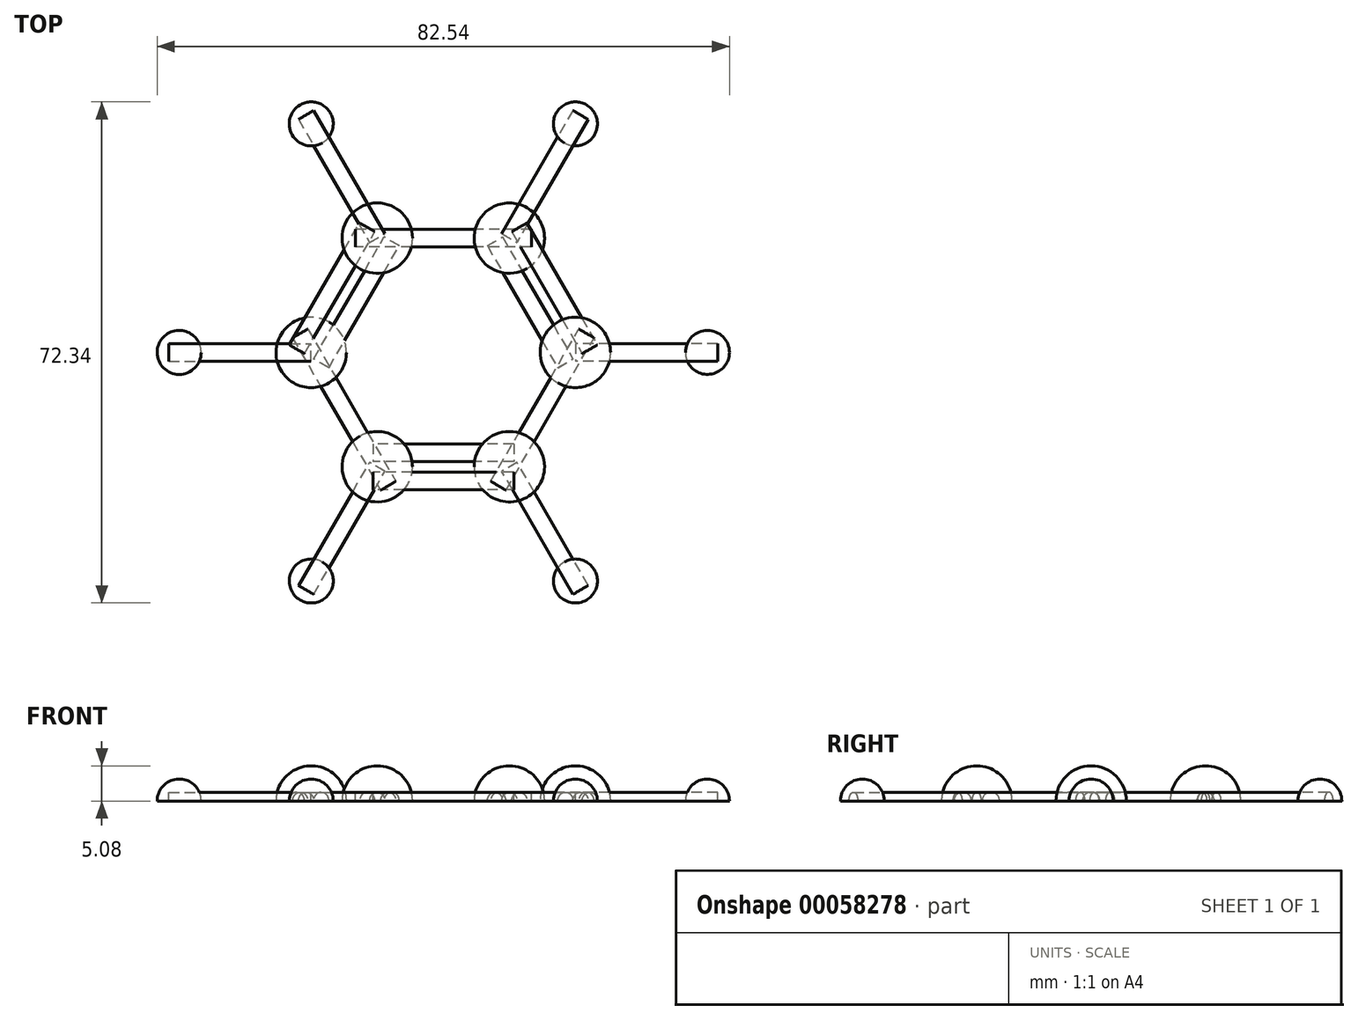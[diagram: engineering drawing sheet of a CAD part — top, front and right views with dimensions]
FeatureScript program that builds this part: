
annotation { "Feature Type Name" : "Feature", "Feature Type Description" : "" }
export const myFeature = defineFeature(function(context is Context, id is Id, definition is map)
    precondition{}
    {
        {
            var Q0;
            Q0=qCreatedBy(makeId("Top.planeOp"),FACE);
            var sketch = newSketch(context, id + "F0", { "sketchPlane" : qUnion([Q0])});
            skCircle(sketch, "E0", {"center": v(-9.53, 16.5) * mm, "radius": 5.08 * mm, "construction": true});
            skCircle(sketch, "E1", {"center": v(9.52, 16.5) * mm, "radius": 5.08 * mm, "construction": true});
            skCircle(sketch, "E2", {"center": v(19.05, 0) * mm, "radius": 5.08 * mm, "construction": true});
            skLineSegment(sketch, "E3", {"start": v(-9.53, 16.5) * mm, "end": v(9.52, 16.5) * mm, "construction": true});
            skLineSegment(sketch, "E4", {"start": v(9.52, 16.5) * mm, "end": v(19.05, 0) * mm, "construction": true});
            skLineSegment(sketch, "E5", {"start": v(19.05, 0) * mm, "end": v(0, 0) * mm, "construction": true});
            skLineSegment(sketch, "E6", {"start": v(9.53, 16.5) * mm, "end": v(0, 0) * mm, "construction": true});
            skLineSegment(sketch, "E7", {"start": v(0, 0) * mm, "end": v(-9.53, 16.5) * mm, "construction": true});
            skLineSegment(sketch, "E8", {"start": v(19.05, 0) * mm, "end": v(38.1, 0) * mm, "construction": true});
            skCircle(sketch, "E9", {"center": v(38.1, 0) * mm, "radius": 3.18 * mm, "construction": true});
            skSolve(sketch);
        }
        {
            var Q0;
            Q0=qCreatedBy(makeId("Top.planeOp"),FACE);
            var sketch = newSketch(context, id + "F1", { "sketchPlane" : qUnion([Q0])});
            skArc(sketch, "E10", {"start": v(-14.6, 16.5) * mm, "mid": v(-9.53, 11.42) * mm, "end": v(-4.45, 16.5) * mm});
            skLineSegment(sketch, "E11", {"start": v(-4.45, 16.5) * mm, "end": v(-14.6, 16.5) * mm});
            skSolve(sketch);
        }
        {
            var Q0;
            Q0=makeQuery(id+"F1.imprint","IMPRINT",FACE,{"disambiguationData":[TD([[makeQuery(id+"F1.imprint","IMPRINT",EDGE,{"derivedFrom":sQuery(id+"F1.wireOp",EDGE,"E10")}),1.0]])]});
            var Q1;
            Q1=sQuery(id+"F1.wireOp",EDGE,"E11");
            revolve(context, id + "F2", {"entities" : qUnion([Q0]), "axis" : qUnion([Q1]), "revolveType" : RevolveType.FULL});
        }
        {
            var Q0;
            Q0=qCreatedBy(makeId("Front.planeOp"),FACE);
            var sketch = newSketch(context, id + "F3", { "sketchPlane" : qUnion([Q0])});
            skLineSegment(sketch, "E12", {"start": v(0, 0) * mm, "end": v(0, 25.4) * mm, "construction": true});
            skSolve(sketch);
        }
        {
            var Q0;
            Q0=makeQuery(id+"F2.opRevolve","SWEPT_BODY",BODY,{"disambiguationData":[OSD([sQuery(id+"F1.wireOp",EDGE,"E10"),sQuery(id+"F1.wireOp",EDGE,"E11")])]});
            var Q1;
            Q1=sQuery(id+"F3.wireOp",EDGE,"E12");
            circularPattern(context, id + "F4", {"entities" : qUnion([Q0]), "axis" : qUnion([Q1]), "angle" : 60 * degree, "instanceCount" : 6, "oppositeDirection" : true});
        }
        {
            var Q0;
            Q0=qCreatedBy(makeId("Top.planeOp"),FACE);
            var sketch = newSketch(context, id + "F5", { "sketchPlane" : qUnion([Q0])});
            skArc(sketch, "E13", {"start": v(34.92, 0) * mm, "mid": v(38.1, -3.17) * mm, "end": v(41.27, 0) * mm});
            skLineSegment(sketch, "E14", {"start": v(34.92, 0) * mm, "end": v(41.27, 0) * mm});
            skSolve(sketch);
        }
        {
            var Q0;
            Q0=makeQuery(id+"F5.imprint","IMPRINT",FACE,{"disambiguationData":[TD([[makeQuery(id+"F5.imprint","IMPRINT",EDGE,{"derivedFrom":sQuery(id+"F5.wireOp",EDGE,"E13")}),1.0]])]});
            var Q1;
            Q1=sQuery(id+"F5.wireOp",EDGE,"E14");
            revolve(context, id + "F6", {"entities" : qUnion([Q0]), "axis" : qUnion([Q1]), "revolveType" : RevolveType.FULL});
        }
        {
            var Q0;
            Q0=makeQuery(id+"F6.opRevolve","SWEPT_BODY",BODY,{"disambiguationData":[OSD([sQuery(id+"F5.wireOp",EDGE,"E13"),sQuery(id+"F5.wireOp",EDGE,"E14")])]});
            var Q1;
            Q1=sQuery(id+"F3.wireOp",EDGE,"E12");
            circularPattern(context, id + "F7", {"entities" : qUnion([Q0]), "axis" : qUnion([Q1]), "angle" : 60 * degree, "instanceCount" : 6});
        }
        {
            var Q0;
            Q0=qCreatedBy(makeId("Right.planeOp"),FACE);
            var sketch = newSketch(context, id + "F8", { "sketchPlane" : qUnion([Q0])});
            skCircle(sketch, "E15", {"center": v(0, 0) * mm, "radius": 1.27 * mm});
            skSolve(sketch);
        }
        {
            var Q0;
            Q0 = qSketchRegion(id + "F8", true);
            extrude(context, id + "F9", {"entities" : qUnion([Q0]), "depth" : 39.6 * mm, "hasSecondDirection" : true, "secondDirectionOppositeDirection" : false, "secondDirectionDepth" : 19.06 * mm});
        }
        {
            var Q0;
            Q0=makeQuery(id+"F9.opExtrude","SWEPT_BODY",BODY,{"disambiguationData":[OSD([sQuery(id+"F8.wireOp",EDGE,"E15")])]});
            var Q1;
            Q1=sQuery(id+"F3.wireOp",EDGE,"E12");
            circularPattern(context, id + "F10", {"entities" : qUnion([Q0]), "axis" : qUnion([Q1]), "angle" : 60 * degree, "instanceCount" : 6});
        }
        {
            var Q0;
            Q0=qCreatedBy(makeId("Right.planeOp"),FACE);
            var sketch = newSketch(context, id + "F11", { "sketchPlane" : qUnion([Q0])});
            skCircle(sketch, "E16", {"center": v(16.5, 0) * mm, "radius": 1.27 * mm});
            skLineSegment(sketch, "E17", {"start": v(16.5, 0) * mm, "end": v(0, 0) * mm, "construction": true});
            skSolve(sketch);
        }
        {
            var Q0;
            Q0 = qSketchRegion(id + "F11", true);
            var Q1;
            Q1=sQuery(id+"F11.wireOp",EDGE,"E16");
            extrude(context, id + "F12", {"entities" : qUnion([Q0]), "surfaceEntities" : qUnion([Q1]), "endBound" : BoundingType.SYMMETRIC, "depth" : 25.4 * mm});
        }
        {
            var Q0;
            Q0=makeQuery(id+"F12.opExtrude","SWEPT_BODY",BODY,{"disambiguationData":[OSD([sQuery(id+"F11.wireOp",EDGE,"E16")])]});
            var Q1;
            Q1=sQuery(id+"F3.wireOp",EDGE,"E12");
            circularPattern(context, id + "F13", {"entities" : qUnion([Q0]), "axis" : qUnion([Q1]), "angle" : 120 * degree, "instanceCount" : 3});
        }
        {
            var Q0;
            Q0=qCreatedBy(makeId("Right.planeOp"),FACE);
            var sketch = newSketch(context, id + "F14", { "sketchPlane" : qUnion([Q0])});
            skLineSegment(sketch, "E18", {"start": v(0, 0) * mm, "end": v(-16.5, 0) * mm, "construction": true});
            skCircle(sketch, "E19", {"center": v(-18.53, 0) * mm, "radius": 1.27 * mm});
            skCircle(sketch, "E20", {"center": v(-14.47, 0) * mm, "radius": 1.27 * mm});
            skLineSegment(sketch, "E21", {"start": v(-14.47, 0) * mm, "end": v(-16.5, 0) * mm, "construction": true});
            skLineSegment(sketch, "E22", {"start": v(-16.5, 0) * mm, "end": v(-18.53, 0) * mm, "construction": true});
            skSolve(sketch);
        }
        {
            var Q0;
            Q0=makeQuery(id+"F14.imprint","IMPRINT",FACE,{"disambiguationData":[TD([[makeQuery(id+"F14.imprint","IMPRINT",EDGE,{"derivedFrom":sQuery(id+"F14.wireOp",EDGE,"E20")}),1.0]])]});
            var Q1;
            Q1=makeQuery(id+"F14.imprint","IMPRINT",FACE,{"disambiguationData":[TD([[makeQuery(id+"F14.imprint","IMPRINT",EDGE,{"derivedFrom":sQuery(id+"F14.wireOp",EDGE,"E19")}),1.0]])]});
            extrude(context, id + "F15", {"entities" : qUnion([Q0, Q1]), "endBound" : BoundingType.SYMMETRIC, "depth" : 20.32 * mm});
        }
        {
            var Q0;
            Q0=makeQuery(id+"F15.opExtrude","SWEPT_BODY",BODY,{"disambiguationData":[OSD([sQuery(id+"F14.wireOp",EDGE,"E19")])]});
            var Q1;
            Q1=sQuery(id+"F3.wireOp",EDGE,"E12");
            circularPattern(context, id + "F16", {"entities" : qUnion([Q0]), "axis" : qUnion([Q1]), "angle" : 120 * degree, "instanceCount" : 3});
        }
        {
            var Q0;
            Q0=makeQuery(id+"F15.opExtrude","SWEPT_BODY",BODY,{"disambiguationData":[OSD([sQuery(id+"F14.wireOp",EDGE,"E20")])]});
            var Q1;
            Q1=sQuery(id+"F3.wireOp",EDGE,"E12");
            circularPattern(context, id + "F17", {"entities" : qUnion([Q0]), "axis" : qUnion([Q1]), "angle" : 120 * degree, "instanceCount" : 3});
        }
        {
            var Q0;
            Q0=qCreatedBy(makeId("Top.planeOp"),FACE);
            var sketch = newSketch(context, id + "F18", { "sketchPlane" : qUnion([Q0])});
            skCircle(sketch, "E23", {"center": v(0, 0) * mm, "radius": 45.18 * mm});
            skSolve(sketch);
        }
        {
            var Q0;
            Q0=makeQuery(id+"F18.imprint","IMPRINT",FACE,{"disambiguationData":[TD([[makeQuery(id+"F18.imprint","IMPRINT",EDGE,{"derivedFrom":sQuery(id+"F18.wireOp",EDGE,"E23")}),1.0]])]});
            extrude(context, id + "F19", {"entities" : qUnion([Q0]), "operationType" : NewBodyOperationType.REMOVE, "oppositeDirection" : true, "depth" : 9.7 * mm});
        }
    });
